# Revit family: NBS_BetafenceLimited_MtlMeshPnlFncngSym_Nylofor2DSuper-Twilfix
name_source: partatom
category: Site
revit_build: Autodesk Revit 2017 (Build: 20171027_0315(x64)
units: mm (PartAtom-declared; Revit-internal decimal feet)

## family parameters
Cut with Voids When Loaded = No
Part Type = Normal
Round Connector Dimension = Use Diameter
Shared = No

## types (1)
- Nylofor 2D Super + Twilfix
    Applications = Factories and logistics, high security, public spaces and buildings, sports infra-structure
    AssetType = Fixed
    BIMObjectName = NBS_BetafenceLimited_MetalMeshPanelFencingSystem_Nylofor2DSuper-Twilfix
    Category = Ss_25_14_67_51: Metal mesh panel fencing systems
    Color = Green (RAL 6005), black (RAL 9005), grey (RAL 6005)
    Diameter = 0 mm  [stored 0 ft]
    DurationUnit = year
    Finish = Polyester coating
    FoundationMaterial = NBS_Concept
    Functionalities = Dissuasion, delay
    Gradient01Maximum = 4.00%
    Gradient01PostAxisDistance = 2500 mm  [stored 8.2021 ft]
    Gradient02Maximum = 5.00%
    Gradient02PostAxisDistance = 2000 mm  [stored 6.56168 ft]
    Gradient03Maximum = 6.67%
    Gradient03PostAxisDistance = 1500 mm
    Gradient04Maximum = 10.00%
    Gradient04PostAxisDistance = 1000 mm  [stored 3.28084 ft]
    GradientMaximumPostAxisDistance = 1000 mm  [stored 3.28084 ft]
    Height = 2430 mm  [stored 7.97244 ft]
    IfcExportAs = IfcWallType
    IfcExportType = NOTDEFINED
    IsExternal = Yes
    ManufacturerName = Betafence Limited
    ManufacturerURL = www.betafence.co.uk
    MaximumIncline = 10.00%
    ModelReference = Nylofor 2D Super + Twilfix
    NBSCertification = www.nationalbimlibrary.com/cert/ryyzswgp
    NBSDescription = Metal mesh panel fencing system
    NBSReference = 25-20-30/145
    Name = MetalMeshPanelFencingSystem_Nylofor2DSuperTwilfix_BetafenceLimited
    NominalHeight = 2430 mm  [stored 7.97244 ft]
    NominalLength = 0 mm  [stored 0 ft]
    NominalWidth = 2500 mm  [stored 8.2021 ft]
    PanelElevationAboveFoundation = 260 mm  [stored 0.853018 ft]
    PanelHeight = 2430 mm  [stored 7.97244 ft]
    PanelMaterial = NBS_BetafenceLimited_MtlMeshPnlFncngSym_Nylofor2DSuper_Panel
    PanelMaterialThickness = 45 mm  [stored 0.147638 ft]
    PanelOffsetFromPost = 8 mm  [stored 0.0262467 ft]
    PanelOffsetFromPostCL = 50 mm  [stored 0.164042 ft]
    PanelSizeOptions = 2500 x 630 mm, 2500 x 830 mm, 2500 x 1030 mm, 2500 x 1230 mm, 2500 x 1430 mm, 2500 x 1630 mm, 2500 x 1830 mm, 2500 x 2030 mm, 2500 x 2230 mm, 2500 x 2430 mm, 2500 x 3000 mm
    PanelThickness = 20 mm  [stored 0.0656168 ft]
    Panels = Welded mesh panels with double horizontal wires providing high rigidity
    PostFoundations = Installation guides available on request
    PostHeightAboveGround = 2490 mm  [stored 8.16929 ft]
    PostHeightBelowGround = 200 mm  [stored 0.656168 ft]
    PostMaterial = NBS_Concept
    PostThickness = 60 mm  [stored 0.19685 ft]
    PostWidth = 60 mm  [stored 0.19685 ft]
    Posts = Twilfix
    ProductInformation = www.betafence.co.uk/en/nylofor-2d-super
    SecurityLevel = General purpose and security
    SiteAppliedFinishes = Galvanised
    StandardPostAxisDistance = 2500 mm  [stored 8.2021 ft]
    SystemAccessories = Concrete plate holder, cranked extension arm and connection piece or welded cranked arms, security devices
    Uniclass2015Code = Ss_25_14_67_51
    Uniclass2015Title = Metal mesh panel fencing systems
    Uniclass2015Version = Systems v1.13
    Version = 2
    WarrantyDurationUnit = year

note: [stored X ft] marks values corroborated as IEEE doubles in the binary element streams (Revit-internal decimal feet)

## geometry (parser evidence)
native form markers: Sweep x7
no freeform markers — native parametric forms only
